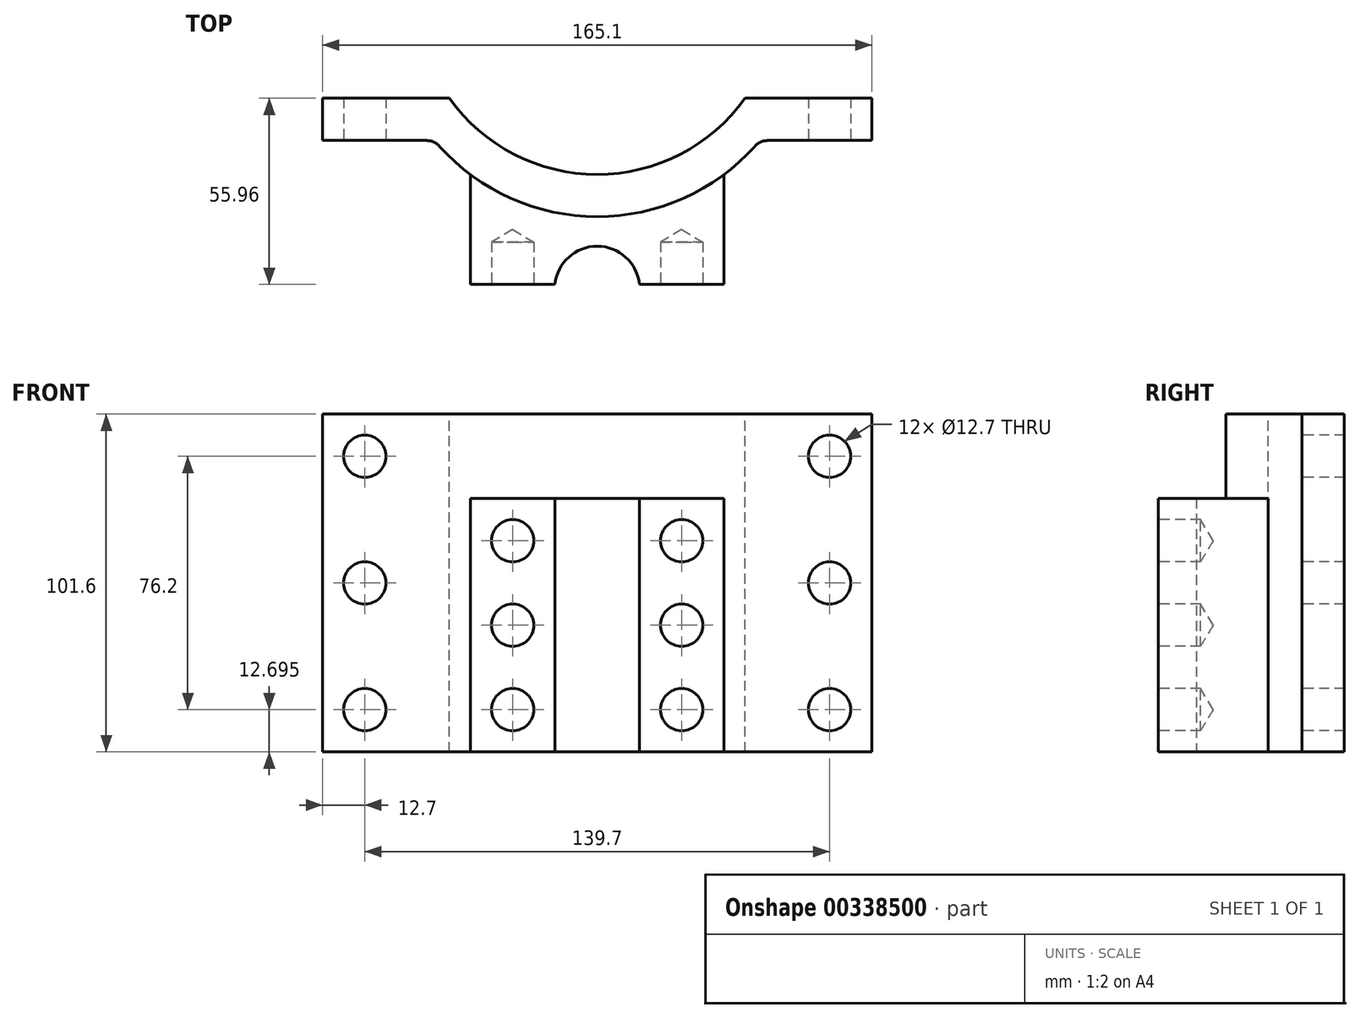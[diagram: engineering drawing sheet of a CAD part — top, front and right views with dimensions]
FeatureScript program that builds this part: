
annotation { "Feature Type Name" : "Feature", "Feature Type Description" : "" }
export const myFeature = defineFeature(function(context is Context, id is Id, definition is map)
    precondition{}
    {
        {
            var Q0;
            Q0=qCreatedBy(makeId("Top.planeOp"),FACE);
            var sketch = newSketch(context, id + "F0", { "sketchPlane" : qUnion([Q0])});
            skCircle(sketch, "E0", {"center": v(0, 0) * mm, "radius": 6.35 * mm});
            skSolve(sketch);
        }
        {
            var Q0;
            Q0=makeQuery(id+"F0.imprint","IMPRINT",FACE,{"disambiguationData":[TD([[makeQuery(id+"F0.imprint","IMPRINT",EDGE,{"derivedFrom":sQuery(id+"F0.wireOp",EDGE,"E0")}),1.0]])]});
            extrude(context, id + "F1", {"entities" : qUnion([Q0]), "oppositeDirection" : true, "depth" : 47.62 * mm});
        }
        {
            var Q0;
            Q0=makeQuery(id+"F1.opExtrude","CAP_FACE",FACE,{"disambiguationData":[OSD([sQuery(id+"F0.wireOp",EDGE,"E0")])],"isStart":true});
            var sketch = newSketch(context, id + "F2", { "sketchPlane" : qUnion([Q0])});
            skLineSegment(sketch, "E1", {"start": v(3.5, 5.3) * mm, "end": v(-3.5, 5.3) * mm});
            skSolve(sketch);
        }
        {
            var Q0;
            {var subQ0=sQuery(id+"F2.wireOp",EDGE,"E1");Q0=makeQuery(id+"F2.imprint","IMPRINT",FACE,{"disambiguationData":[TD([[makeQuery(id+"F2.imprint","IMPRINT",EDGE,{"derivedFrom":subQ0}),-1.0]])]});}
            extrude(context, id + "F3", {"entities" : qUnion([Q0]), "operationType" : NewBodyOperationType.REMOVE, "oppositeDirection" : true, "depth" : 31.75 * mm});
        }
        {
            var Q0;
            Q0=makeQuery(id+"F1.opExtrude","CAP_FACE",FACE,{"disambiguationData":[OSD([sQuery(id+"F0.wireOp",EDGE,"E0")])],"isStart":false});
            var sketch = newSketch(context, id + "F4", { "sketchPlane" : qUnion([Q0])});
            skCircle(sketch, "E2", {"center": v(0, 0) * mm, "radius": 18.73 * mm});
            skCircle(sketch, "E3", {"center": v(0, 0) * mm, "radius": 23.81 * mm});
            skSolve(sketch);
        }
        {
            var Q0;
            Q0=makeQuery(id+"F4.imprint","IMPRINT",FACE,{"disambiguationData":[TD([[makeQuery(id+"F4.imprint","IMPRINT",EDGE,{"derivedFrom":sQuery(id+"F4.wireOp",EDGE,"E2")}),-1.0]])]});
            extrude(context, id + "F5", {"entities" : qUnion([Q0]), "oppositeDirection" : true, "depth" : 20.32 * mm});
        }
        {
            var Q0;
            Q0=makeQuery(id+"F1.opExtrude","CAP_FACE",FACE,{"disambiguationData":[OSD([sQuery(id+"F0.wireOp",EDGE,"E0")])],"isStart":false});
            var sketch = newSketch(context, id + "F6", { "sketchPlane" : qUnion([Q0])});
            skCircle(sketch, "E4", {"center": v(0, 0) * mm, "radius": 54.61 * mm});
            skSolve(sketch);
        }
        {
            var Q0;
            Q0=makeQuery(id+"F6.imprint","IMPRINT",FACE,{"disambiguationData":[TD([[makeQuery(id+"F6.imprint","IMPRINT",EDGE,{"derivedFrom":sQuery(id+"F6.wireOp",EDGE,"E4")}),1.0]])]});
            var Q1;
            Q1=makeQuery(id+"F6.imprint","IMPRINT",FACE,{"disambiguationData":[TD([[makeQuery(id+"F6.imprint","IMPRINT",EDGE,{"derivedFrom":makeQuery(id+"F1.opExtrude","CAP_EDGE",EDGE,{"disambiguationData":[OSD([sQuery(id+"F0.wireOp",EDGE,"E0")])],"isStart":false})}),-1.0]])]});
            extrude(context, id + "F7", {"entities" : qUnion([Q0, Q1]), "depth" : 14.6 * mm});
        }
        {
            var Q0;
            Q0=makeQuery(id+"F7.opExtrude","CAP_FACE",FACE,{"disambiguationData":[OSD([sQuery(id+"F6.wireOp",EDGE,"E4")])],"isStart":false});
            var sketch = newSketch(context, id + "F8", { "sketchPlane" : qUnion([Q0])});
            skCircle(sketch, "E5", {"center": v(0, 0) * mm, "radius": 54.6 * mm});
            skSolve(sketch);
        }
        {
            var Q0;
            Q0=makeQuery(id+"F8.imprint","IMPRINT",FACE,{"disambiguationData":[TD([[makeQuery(id+"F8.imprint","IMPRINT",EDGE,{"derivedFrom":sQuery(id+"F8.wireOp",EDGE,"E5")}),1.0]])]});
            extrude(context, id + "F9", {"entities" : qUnion([Q0]), "operationType" : NewBodyOperationType.ADD, "depth" : 118.5 * mm});
        }
        {
            var Q0;
            Q0=makeQuery(id+"F9.opExtrude","CAP_FACE",FACE,{"disambiguationData":[OSD([sQuery(id+"F8.wireOp",EDGE,"E5")])],"isStart":false});
            var sketch = newSketch(context, id + "F10", { "sketchPlane" : qUnion([Q0])});
            skCircle(sketch, "E6", {"center": v(0, 0) * mm, "radius": 54.61 * mm});
            skSolve(sketch);
        }
        {
            var Q0;
            Q0=makeQuery(id+"F10.imprint","IMPRINT",FACE,{"disambiguationData":[TD([[makeQuery(id+"F10.imprint","IMPRINT",EDGE,{"derivedFrom":sQuery(id+"F10.wireOp",EDGE,"E6")}),1.0]])]});
            var Q1;
            Q1=makeQuery(id+"F10.imprint","IMPRINT",FACE,{"disambiguationData":[TD([[makeQuery(id+"F10.imprint","IMPRINT",EDGE,{"derivedFrom":makeQuery(id+"F9.opExtrude","CAP_EDGE",EDGE,{"disambiguationData":[OSD([sQuery(id+"F8.wireOp",EDGE,"E5")])],"isStart":false})}),1.0]])]});
            extrude(context, id + "F11", {"entities" : qUnion([Q0, Q1]), "operationType" : NewBodyOperationType.ADD, "depth" : 57.15 * mm});
        }
        {
            var Q0;
            Q0=makeQuery(id+"F7.opExtrude","CAP_FACE",FACE,{"disambiguationData":[OSD([sQuery(id+"F6.wireOp",EDGE,"E4")])],"isStart":true});
            var sketch = newSketch(context, id + "F12", { "sketchPlane" : qUnion([Q0])});
            skLineSegment(sketch, "E7", {"start": v(-44.45, 31.72) * mm, "end": v(44.45, 31.72) * mm});
            skPoint(sketch, "E8", {"position": v(0, 54.61) * mm});
            skArc(sketch, "E9", {"start": v(44.45, 31.72) * mm, "mid": v(0, 54.61) * mm, "end": v(-44.45, 31.72) * mm});
            skLineSegment(sketch, "E10", {"start": v(-44.45, 31.72) * mm, "end": v(-82.55, 31.72) * mm});
            skLineSegment(sketch, "E11", {"start": v(44.45, 31.72) * mm, "end": v(82.55, 31.72) * mm});
            skLineSegment(sketch, "E12", {"start": v(0, 54.61) * mm, "end": v(0, 67.31) * mm});
            skLineSegment(sketch, "E13", {"start": v(-82.55, 31.72) * mm, "end": v(-82.55, 44.42) * mm});
            skLineSegment(sketch, "E14", {"start": v(-82.55, 44.42) * mm, "end": v(-48.9, 44.42) * mm});
            skLineSegment(sketch, "E15", {"start": v(82.55, 31.72) * mm, "end": v(82.55, 44.42) * mm});
            skLineSegment(sketch, "E16", {"start": v(82.55, 44.42) * mm, "end": v(48.9, 44.42) * mm});
            skArc(sketch, "E17", {"start": v(48.9, 44.42) * mm, "mid": v(0, 67.31) * mm, "end": v(-48.9, 44.42) * mm});
            skSolve(sketch);
        }
        {
            var Q0;
            {var subQ0=sQuery(id+"F12.wireOp",EDGE,"E10");Q0=makeQuery(id+"F12.imprint","IMPRINT",FACE,{"disambiguationData":[TD([[makeQuery(id+"F12.imprint","IMPRINT",EDGE,{"derivedFrom":subQ0}),-1.0]])]});}
            var Q1;
            {var subQ0=sQuery(id+"F12.wireOp",EDGE,"E11");Q1=makeQuery(id+"F12.imprint","IMPRINT",FACE,{"disambiguationData":[TD([[makeQuery(id+"F12.imprint","IMPRINT",EDGE,{"derivedFrom":subQ0}),1.0]])]});}
            extrude(context, id + "F13", {"entities" : qUnion([Q0, Q1]), "oppositeDirection" : true, "depth" : 101.6 * mm});
        }
        {
            var Q0;
            Q0=makeQuery(id+"F7.opExtrude","CAP_FACE",FACE,{"disambiguationData":[OSD([sQuery(id+"F6.wireOp",EDGE,"E4")])],"isStart":true});
            var sketch = newSketch(context, id + "F14", { "sketchPlane" : qUnion([Q0])});
            skLineSegment(sketch, "E18", {"start": v(-44.45, -31.72) * mm, "end": v(44.45, -31.72) * mm});
            skPoint(sketch, "E19", {"position": v(0, -54.61) * mm});
            skArc(sketch, "E20", {"start": v(-44.45, -31.72) * mm, "mid": v(0, -54.61) * mm, "end": v(44.45, -31.72) * mm});
            skLineSegment(sketch, "E21", {"start": v(-44.45, -31.72) * mm, "end": v(-82.55, -31.72) * mm});
            skLineSegment(sketch, "E22", {"start": v(44.45, -31.72) * mm, "end": v(82.55, -31.72) * mm});
            skLineSegment(sketch, "E23", {"start": v(0, -54.61) * mm, "end": v(0, -67.31) * mm});
            skLineSegment(sketch, "E24", {"start": v(-82.55, -31.72) * mm, "end": v(-82.55, -44.42) * mm});
            skLineSegment(sketch, "E25", {"start": v(-82.55, -44.42) * mm, "end": v(-48.9, -44.42) * mm});
            skLineSegment(sketch, "E26", {"start": v(82.55, -31.72) * mm, "end": v(82.55, -44.42) * mm});
            skLineSegment(sketch, "E27", {"start": v(82.55, -44.42) * mm, "end": v(48.9, -44.42) * mm});
            skArc(sketch, "E28", {"start": v(-48.9, -44.42) * mm, "mid": v(0, -67.31) * mm, "end": v(48.9, -44.42) * mm});
            skSolve(sketch);
        }
        {
            var Q0;
            {var subQ0=sQuery(id+"F14.wireOp",EDGE,"E22");Q0=makeQuery(id+"F14.imprint","IMPRINT",FACE,{"disambiguationData":[TD([[makeQuery(id+"F14.imprint","IMPRINT",EDGE,{"derivedFrom":subQ0}),-1.0]])]});}
            var Q1;
            {var subQ0=sQuery(id+"F14.wireOp",EDGE,"E21");Q1=makeQuery(id+"F14.imprint","IMPRINT",FACE,{"disambiguationData":[TD([[makeQuery(id+"F14.imprint","IMPRINT",EDGE,{"derivedFrom":subQ0}),1.0]])]});}
            extrude(context, id + "F15", {"entities" : qUnion([Q0, Q1]), "oppositeDirection" : true, "depth" : 25.4 * mm});
        }
        {
            var Q0;
            {var subQ0=sQuery(id+"F14.wireOp",EDGE,"E25");var subQ2=sQuery(id+"F14.wireOp",EDGE,"E20");var subQ3=sQuery(id+"F14.wireOp",EDGE,"E21");var subQ4=sQuery(id+"F14.wireOp",EDGE,"E24");var subQ5=sQuery(id+"F14.wireOp",EDGE,"E28");Q0=makeQuery(id+"Fq8fBj3KPbGBi3Q_5.boolean.opBoolean","SPLIT",FACE,{"disambiguationData":[TD([makeQuery(id+"F15.opExtrude","SWEPT_FACE",FACE,{"disambiguationData":[OSD([subQ3])]})])],"derivedFrom":makeQuery(id+"F15.opExtrude","CAP_FACE",FACE,{"disambiguationData":[OSD([subQ2,subQ3,sQuery(id+"F14.wireOp",EDGE,"E22"),subQ4,subQ0,sQuery(id+"F14.wireOp",EDGE,"E26"),sQuery(id+"F14.wireOp",EDGE,"E27"),subQ5])],"isStart":false})});}
            var Q1;
            {var subQ0=sQuery(id+"F14.wireOp",EDGE,"E27");var subQ1=sQuery(id+"F14.wireOp",EDGE,"E26");var subQ2=sQuery(id+"F14.wireOp",EDGE,"E22");var subQ3=sQuery(id+"F14.wireOp",EDGE,"E20");var subQ4=sQuery(id+"F14.wireOp",EDGE,"E28");Q1=makeQuery(id+"Fq8fBj3KPbGBi3Q_5.boolean.opBoolean","SPLIT",FACE,{"disambiguationData":[TD([makeQuery(id+"F15.opExtrude","SWEPT_FACE",FACE,{"disambiguationData":[OSD([subQ2])]})])],"derivedFrom":makeQuery(id+"F15.opExtrude","CAP_FACE",FACE,{"disambiguationData":[OSD([subQ3,sQuery(id+"F14.wireOp",EDGE,"E21"),subQ2,sQuery(id+"F14.wireOp",EDGE,"E24"),sQuery(id+"F14.wireOp",EDGE,"E25"),subQ1,subQ0,subQ4])],"isStart":false})});}
            extrude(context, id + "F16", {"entities" : qUnion([Q0, Q1]), "operationType" : NewBodyOperationType.ADD, "depth" : 76.2 * mm});
        }
        {
            var Q0;
            Q0=makeQuery(id+"F16.opExtrude","CAP_FACE",FACE,{"disambiguationData":[OSD([sQuery(id+"F14.wireOp",EDGE,"E20"),sQuery(id+"F14.wireOp",EDGE,"E21"),sQuery(id+"F14.wireOp",EDGE,"E22"),sQuery(id+"F14.wireOp",EDGE,"E24"),sQuery(id+"F14.wireOp",EDGE,"E25"),sQuery(id+"F14.wireOp",EDGE,"E26"),sQuery(id+"F14.wireOp",EDGE,"E27"),sQuery(id+"F14.wireOp",EDGE,"E28")])],"isStart":false});
            var sketch = newSketch(context, id + "F17", { "sketchPlane" : qUnion([Q0])});
            skPoint(sketch, "E29", {"position": v(0, 67.31) * mm});
            skLineSegment(sketch, "E30", {"start": v(-38.1, 54.66) * mm, "end": v(-38.1, 87.68) * mm});
            skLineSegment(sketch, "E31", {"start": v(38.1, 54.66) * mm, "end": v(38.1, 87.68) * mm});
            skLineSegment(sketch, "E32", {"start": v(38.1, 87.68) * mm, "end": v(12.7, 87.68) * mm});
            skPoint(sketch, "E33", {"position": v(0, 76.2) * mm});
            skLineSegment(sketch, "E34", {"start": v(-38.1, 87.68) * mm, "end": v(-12.7, 87.68) * mm});
            skArc(sketch, "E35", {"start": v(-12.7, 87.68) * mm, "mid": v(0, 76.2) * mm, "end": v(12.7, 87.68) * mm});
            skSolve(sketch);
        }
        {
            var Q0;
            {var subQ0=sQuery(id+"F17.wireOp",EDGE,"E30");Q0=makeQuery(id+"F17.imprint","IMPRINT",FACE,{"disambiguationData":[TD([[makeQuery(id+"F17.imprint","IMPRINT",EDGE,{"derivedFrom":subQ0}),-1.0]])]});}
            extrude(context, id + "F18", {"entities" : qUnion([Q0]), "operationType" : NewBodyOperationType.ADD, "oppositeDirection" : true, "depth" : 76.2 * mm});
        }
        {
            var Q0;
            Q0=makeQuery(id+"F18.opExtrude","SWEPT_FACE",FACE,{"disambiguationData":[OSD([sQuery(id+"F17.wireOp",EDGE,"E34")])]});
            var sketch = newSketch(context, id + "F19", { "sketchPlane" : qUnion([Q0])});
            skCircle(sketch, "E36", {"center": v(-25.4, -85.72) * mm, "radius": 6.35 * mm});
            skCircle(sketch, "E37", {"center": v(-25.4, -111.12) * mm, "radius": 6.35 * mm});
            skCircle(sketch, "E38", {"center": v(-25.4, -136.53) * mm, "radius": 6.35 * mm});
            skCircle(sketch, "E39", {"center": v(25.4, -85.72) * mm, "radius": 6.35 * mm});
            skCircle(sketch, "E40", {"center": v(25.4, -111.12) * mm, "radius": 6.35 * mm});
            skCircle(sketch, "E41", {"center": v(25.4, -136.53) * mm, "radius": 6.35 * mm});
            skSolve(sketch);
        }
        {
            var Q0;
            Q0=sQuery(id+"F19.wireOp",VERTEX,"E36.center");
            var Q1;
            Q1=sQuery(id+"F19.wireOp",VERTEX,"E39.center");
            var Q2;
            Q2=sQuery(id+"F19.wireOp",VERTEX,"E37.center");
            var Q3;
            Q3=sQuery(id+"F19.wireOp",VERTEX,"E40.center");
            var Q4;
            Q4=sQuery(id+"F19.wireOp",VERTEX,"E38.center");
            var Q5;
            Q5=sQuery(id+"F19.wireOp",VERTEX,"E41.center");
            var Q6;
            Q6=makeQuery(id+"F15.opExtrude","SWEPT_BODY",BODY,{"disambiguationData":[OSD([sQuery(id+"F14.wireOp",EDGE,"E20"),sQuery(id+"F14.wireOp",EDGE,"E21"),sQuery(id+"F14.wireOp",EDGE,"E22"),sQuery(id+"F14.wireOp",EDGE,"E24"),sQuery(id+"F14.wireOp",EDGE,"E25"),sQuery(id+"F14.wireOp",EDGE,"E26"),sQuery(id+"F14.wireOp",EDGE,"E27"),sQuery(id+"F14.wireOp",EDGE,"E28")])]});
            hole(context, id + "F20", {"style" : HoleStyle.SIMPLE, "endStyle" : HoleEndStyle.BLIND, "holeDiameter" : 12.7 * mm, "holeDepth" : 12.7 * mm, "isTappedThrough" : true, "tappedDepth" : 12.7 * mm, "tapClearance" : 3, "startFromSketch" : true, "locations" : qUnion([Q0, Q1, Q2, Q3, Q4, Q5]), "scope" : qUnion([Q6])});
        }
        {
            var Q0;
            {var subQ0=sQuery(id+"F14.wireOp",EDGE,"E25");Q0=makeQuery(id+"F16.boolean.opBoolean","MERGE",FACE,{"derivedFrom":[makeQuery(id+"F15.opExtrude","SWEPT_FACE",FACE,{"disambiguationData":[OSD([subQ0])]}),makeQuery(id+"F16.opExtrude","SWEPT_FACE",FACE,{"disambiguationData":[OSD([subQ0])]})]});}
            var sketch = newSketch(context, id + "F21", { "sketchPlane" : qUnion([Q0])});
            skCircle(sketch, "E42", {"center": v(-69.85, -60.33) * mm, "radius": 6.35 * mm});
            skCircle(sketch, "E43", {"center": v(-69.85, -98.42) * mm, "radius": 6.35 * mm});
            skCircle(sketch, "E44", {"center": v(-69.85, -136.53) * mm, "radius": 6.35 * mm});
            skCircle(sketch, "E45", {"center": v(69.85, -60.33) * mm, "radius": 6.35 * mm});
            skCircle(sketch, "E46", {"center": v(69.85, -98.42) * mm, "radius": 6.35 * mm});
            skCircle(sketch, "E47", {"center": v(69.85, -136.53) * mm, "radius": 6.35 * mm});
            skSolve(sketch);
        }
        {
            var Q0;
            Q0=sQuery(id+"F21.wireOp",VERTEX,"E42.center");
            var Q1;
            Q1=sQuery(id+"F21.wireOp",VERTEX,"E43.center");
            var Q2;
            Q2=sQuery(id+"F21.wireOp",VERTEX,"E44.center");
            var Q3;
            Q3=sQuery(id+"F21.wireOp",VERTEX,"E45.center");
            var Q4;
            Q4=sQuery(id+"F21.wireOp",VERTEX,"E46.center");
            var Q5;
            Q5=sQuery(id+"F21.wireOp",VERTEX,"E47.center");
            var Q6;
            Q6=makeQuery(id+"F15.opExtrude","SWEPT_BODY",BODY,{"disambiguationData":[OSD([sQuery(id+"F14.wireOp",EDGE,"E20"),sQuery(id+"F14.wireOp",EDGE,"E21"),sQuery(id+"F14.wireOp",EDGE,"E22"),sQuery(id+"F14.wireOp",EDGE,"E24"),sQuery(id+"F14.wireOp",EDGE,"E25"),sQuery(id+"F14.wireOp",EDGE,"E26"),sQuery(id+"F14.wireOp",EDGE,"E27"),sQuery(id+"F14.wireOp",EDGE,"E28")])]});
            var Q7;
            Q7=makeQuery(id+"F13.opExtrude","SWEPT_BODY",BODY,{"disambiguationData":[OSD([sQuery(id+"F12.wireOp",EDGE,"E9"),sQuery(id+"F12.wireOp",EDGE,"E10"),sQuery(id+"F12.wireOp",EDGE,"E11"),sQuery(id+"F12.wireOp",EDGE,"E13"),sQuery(id+"F12.wireOp",EDGE,"E14"),sQuery(id+"F12.wireOp",EDGE,"E15"),sQuery(id+"F12.wireOp",EDGE,"E16"),sQuery(id+"F12.wireOp",EDGE,"E17")])]});
            hole(context, id + "F22", {"style" : HoleStyle.SIMPLE, "endStyle" : HoleEndStyle.THROUGH, "holeDiameter" : 12.7 * mm, "isTappedThrough" : true, "tappedDepth" : 12.7 * mm, "tapClearance" : 3, "startFromSketch" : true, "locations" : qUnion([Q0, Q1, Q2, Q3, Q4, Q5]), "scope" : qUnion([Q6, Q7])});
        }
        {
            var Q0;
            Q0=makeQuery(id+"F18.opExtrude","SWEPT_EDGE",EDGE,{"disambiguationData":[OSD([sQuery(id+"F14.wireOp",EDGE,"E28"),sQuery(id+"F17.wireOp",EDGE,"E30")])]});
            var Q1;
            Q1=makeQuery(id+"F18.opExtrude","CAP_EDGE",EDGE,{"disambiguationData":[OSD([sQuery(id+"F14.wireOp",EDGE,"E28")])],"isStart":false});
            var Q2;
            Q2=makeQuery(id+"F18.opExtrude","SWEPT_EDGE",EDGE,{"disambiguationData":[OSD([sQuery(id+"F14.wireOp",EDGE,"E28"),sQuery(id+"F17.wireOp",EDGE,"E31")])]});
            var Q3;
            {var subQ0=sQuery(id+"F14.wireOp",EDGE,"E28");var subQ1=sQuery(id+"F14.wireOp",EDGE,"E27");Q3=makeQuery(id+"F16.boolean.opBoolean","MERGE",EDGE,{"derivedFrom":[makeQuery(id+"F15.opExtrude","SWEPT_EDGE",EDGE,{"disambiguationData":[OSD([subQ1,subQ0])]}),makeQuery(id+"F16.opExtrude","SWEPT_EDGE",EDGE,{"disambiguationData":[OSD([subQ1,subQ0])]})]});}
            var Q4;
            {var subQ0=sQuery(id+"F14.wireOp",EDGE,"E28");var subQ1=sQuery(id+"F14.wireOp",EDGE,"E25");Q4=makeQuery(id+"F16.boolean.opBoolean","MERGE",EDGE,{"derivedFrom":[makeQuery(id+"F15.opExtrude","SWEPT_EDGE",EDGE,{"disambiguationData":[OSD([subQ1,subQ0])]}),makeQuery(id+"F16.opExtrude","SWEPT_EDGE",EDGE,{"disambiguationData":[OSD([subQ1,subQ0])]})]});}
            var Q5;
            Q5=makeQuery(id+"F13.opExtrude","SWEPT_EDGE",EDGE,{"disambiguationData":[OSD([sQuery(id+"F12.wireOp",EDGE,"E14"),sQuery(id+"F12.wireOp",EDGE,"E17")])]});
            var Q6;
            Q6=makeQuery(id+"F13.opExtrude","SWEPT_EDGE",EDGE,{"disambiguationData":[OSD([sQuery(id+"F12.wireOp",EDGE,"E16"),sQuery(id+"F12.wireOp",EDGE,"E17")])]});
            fillet(context, id + "F23", {"entities" : qUnion([Q0, Q1, Q2, Q3, Q4, Q5, Q6]), "radius" : 5.08 * mm, "tangentPropagation" : true, "allowEdgeOverflow" : false});
        }
        {
            var Q0;
            Q0=makeQuery(id+"F1.opExtrude","SWEPT_BODY",BODY,{"disambiguationData":[OSD([sQuery(id+"F0.wireOp",EDGE,"E0")])]});
            deleteBodies(context, id + "F24", {"entities" : qUnion([Q0])});
        }
        {
            var Q0;
            Q0=makeQuery(id+"F7.opExtrude","SWEPT_BODY",BODY,{"disambiguationData":[OSD([sQuery(id+"F6.wireOp",EDGE,"E4")])]});
            deleteBodies(context, id + "F25", {"entities" : qUnion([Q0])});
        }
        {
            var Q0;
            Q0=makeQuery(id+"F5.opExtrude","SWEPT_BODY",BODY,{"disambiguationData":[OSD([sQuery(id+"F4.wireOp",EDGE,"E2"),sQuery(id+"F4.wireOp",EDGE,"E3")])]});
            deleteBodies(context, id + "F26", {"entities" : qUnion([Q0])});
        }
        {
            var Q0;
            Q0=makeQuery(id+"F13.opExtrude","SWEPT_BODY",BODY,{"disambiguationData":[OSD([sQuery(id+"F12.wireOp",EDGE,"E9"),sQuery(id+"F12.wireOp",EDGE,"E10"),sQuery(id+"F12.wireOp",EDGE,"E11"),sQuery(id+"F12.wireOp",EDGE,"E13"),sQuery(id+"F12.wireOp",EDGE,"E14"),sQuery(id+"F12.wireOp",EDGE,"E15"),sQuery(id+"F12.wireOp",EDGE,"E16"),sQuery(id+"F12.wireOp",EDGE,"E17")])]});
            deleteBodies(context, id + "F27", {"entities" : qUnion([Q0])});
        }
    });
